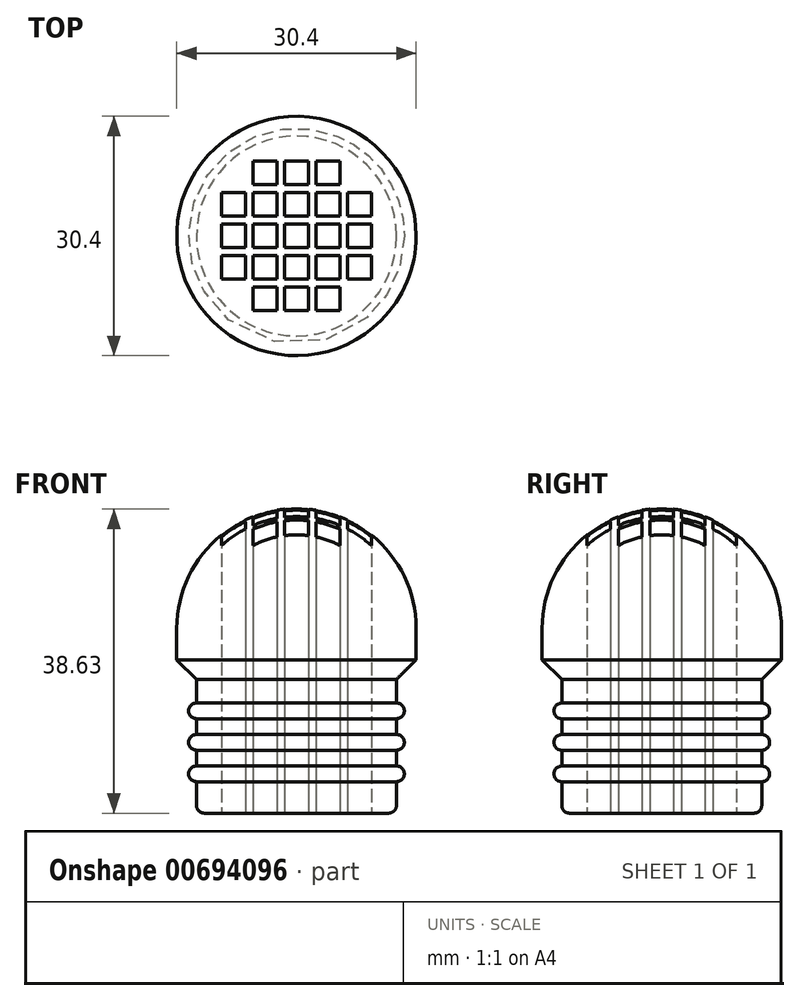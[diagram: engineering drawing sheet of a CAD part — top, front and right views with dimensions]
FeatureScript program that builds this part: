
annotation { "Feature Type Name" : "Feature", "Feature Type Description" : "" }
export const myFeature = defineFeature(function(context is Context, id is Id, definition is map)
    precondition{}
    {
        {
            var Q0;
            Q0=qCreatedBy(makeId("Right.planeOp"),FACE);
            var sketch = newSketch(context, id + "F0", { "sketchPlane" : qUnion([Q0])});
            skLineSegment(sketch, "E0", {"start": v(0, 0) * mm, "end": v(-11.7, 0) * mm});
            skLineSegment(sketch, "E1", {"start": v(-12.7, 1) * mm, "end": v(-12.7, 4) * mm});
            skPoint(sketch, "E2.visualSharp", {"position": v(-12.7, 0) * mm});
            skArc(sketch, "E2.filletArc", {"start": v(-12.7, 1) * mm, "mid": v(-12.4, 0.3) * mm, "end": v(-11.7, 0) * mm});
            skLineSegment(sketch, "E3", {"start": v(-15.2, 23.5) * mm, "end": v(-15.2, 19.5) * mm});
            skLineSegment(sketch, "E4", {"start": v(-15.2, 19.5) * mm, "end": v(-12.7, 17) * mm});
            skArc(sketch, "E5", {"start": v(-15.2, 23.5) * mm, "mid": v(-10.75, 34.25) * mm, "end": v(0, 38.7) * mm});
            skLineSegment(sketch, "E6", {"start": v(0, 38.7) * mm, "end": v(0, 0) * mm});
            skLineSegment(sketch, "E7", {"start": v(-12.7, 14) * mm, "end": v(-12.7, 17) * mm});
            skLineSegment(sketch, "E8", {"start": v(-12.7, 10) * mm, "end": v(-12.7, 12) * mm});
            skLineSegment(sketch, "E9", {"start": v(-12.7, 6) * mm, "end": v(-12.7, 8) * mm});
            skArc(sketch, "E10", {"start": v(-12.7, 14) * mm, "mid": v(-13.7, 13) * mm, "end": v(-12.7, 12) * mm});
            skArc(sketch, "E11", {"start": v(-12.7, 10) * mm, "mid": v(-13.7, 9) * mm, "end": v(-12.7, 8) * mm});
            skArc(sketch, "E12", {"start": v(-12.7, 6) * mm, "mid": v(-13.7, 5) * mm, "end": v(-12.7, 4) * mm});
            skSolve(sketch);
        }
        {
            var Q0;
            Q0 = qSketchRegion(id + "F0", true);
            var Q1;
            Q1 = qConstructionFilter(qBodyType(qCreatedBy(id + "F0" ,EDGE), BodyType.WIRE), ConstructionObject.NO);
            var Q2;
            Q2=sQuery(id+"F0.wireOp",EDGE,"E6");
            revolve(context, id + "F1", {"entities" : qUnion([Q0]), "surfaceEntities" : qUnion([Q1]), "axis" : qUnion([Q2]), "revolveType" : RevolveType.FULL});
        }
        {
            var Q0;
            Q0=makeQuery(id+"F1.opRevolve","SWEPT_FACE",FACE,{"disambiguationData":[OSD([sQuery(id+"F0.wireOp",EDGE,"E0")])]});
            var sketch = newSketch(context, id + "F2", { "sketchPlane" : qUnion([Q0])});
            skLineSegment(sketch, "E13.bottom", {"start": v(-9.5, -6.5) * mm, "end": v(-6.5, -6.5) * mm, "construction": true});
            skLineSegment(sketch, "E13.top", {"start": v(-9.5, -9.5) * mm, "end": v(-6.5, -9.5) * mm, "construction": true});
            skLineSegment(sketch, "E13.left", {"start": v(-9.5, -6.5) * mm, "end": v(-9.5, -9.5) * mm, "construction": true});
            skLineSegment(sketch, "E13.right", {"start": v(-6.5, -6.5) * mm, "end": v(-6.5, -9.5) * mm, "construction": true});
            skPoint(sketch, "E13.middle", {"position": v(-8, -8) * mm});
            skPoint(sketch, "E14.0.1.0", {"position": v(-8, -4) * mm});
            skLineSegment(sketch, "E14.0.1.1", {"start": v(-6.5, -2.5) * mm, "end": v(-6.5, -5.5) * mm});
            skLineSegment(sketch, "E14.0.1.2", {"start": v(-9.5, -5.5) * mm, "end": v(-6.5, -5.5) * mm});
            skLineSegment(sketch, "E14.0.1.3", {"start": v(-9.5, -2.5) * mm, "end": v(-6.5, -2.5) * mm});
            skLineSegment(sketch, "E14.0.1.4", {"start": v(-9.5, -2.5) * mm, "end": v(-9.5, -5.5) * mm});
            skPoint(sketch, "E14.0.2.0", {"position": v(-8, 0) * mm});
            skLineSegment(sketch, "E14.0.2.1", {"start": v(-6.5, 1.5) * mm, "end": v(-6.5, -1.5) * mm});
            skLineSegment(sketch, "E14.0.2.2", {"start": v(-9.5, -1.5) * mm, "end": v(-6.5, -1.5) * mm});
            skLineSegment(sketch, "E14.0.2.3", {"start": v(-9.5, 1.5) * mm, "end": v(-6.5, 1.5) * mm});
            skLineSegment(sketch, "E14.0.2.4", {"start": v(-9.5, 1.5) * mm, "end": v(-9.5, -1.5) * mm});
            skPoint(sketch, "E14.0.3.0", {"position": v(-8, 4) * mm});
            skLineSegment(sketch, "E14.0.3.1", {"start": v(-6.5, 5.5) * mm, "end": v(-6.5, 2.5) * mm});
            skLineSegment(sketch, "E14.0.3.2", {"start": v(-9.5, 2.5) * mm, "end": v(-6.5, 2.5) * mm});
            skLineSegment(sketch, "E14.0.3.3", {"start": v(-9.5, 5.5) * mm, "end": v(-6.5, 5.5) * mm});
            skLineSegment(sketch, "E14.0.3.4", {"start": v(-9.5, 5.5) * mm, "end": v(-9.5, 2.5) * mm});
            skPoint(sketch, "E14.0.4.0", {"position": v(-8, 8) * mm});
            skLineSegment(sketch, "E14.0.4.1", {"start": v(-6.5, 9.5) * mm, "end": v(-6.5, 6.5) * mm, "construction": true});
            skLineSegment(sketch, "E14.0.4.2", {"start": v(-9.5, 6.5) * mm, "end": v(-6.5, 6.5) * mm, "construction": true});
            skLineSegment(sketch, "E14.0.4.3", {"start": v(-9.5, 9.5) * mm, "end": v(-6.5, 9.5) * mm, "construction": true});
            skLineSegment(sketch, "E14.0.4.4", {"start": v(-9.5, 9.5) * mm, "end": v(-9.5, 6.5) * mm, "construction": true});
            skPoint(sketch, "E14.1.0.0", {"position": v(-4, -8) * mm});
            skLineSegment(sketch, "E14.1.0.1", {"start": v(-2.5, -6.5) * mm, "end": v(-2.5, -9.5) * mm});
            skLineSegment(sketch, "E14.1.0.2", {"start": v(-5.5, -9.5) * mm, "end": v(-2.5, -9.5) * mm});
            skLineSegment(sketch, "E14.1.0.3", {"start": v(-5.5, -6.5) * mm, "end": v(-2.5, -6.5) * mm});
            skLineSegment(sketch, "E14.1.0.4", {"start": v(-5.5, -6.5) * mm, "end": v(-5.5, -9.5) * mm});
            skPoint(sketch, "E14.1.1.0", {"position": v(-4, -4) * mm});
            skLineSegment(sketch, "E14.1.1.1", {"start": v(-2.5, -2.5) * mm, "end": v(-2.5, -5.5) * mm});
            skLineSegment(sketch, "E14.1.1.2", {"start": v(-5.5, -5.5) * mm, "end": v(-2.5, -5.5) * mm});
            skLineSegment(sketch, "E14.1.1.3", {"start": v(-5.5, -2.5) * mm, "end": v(-2.5, -2.5) * mm});
            skLineSegment(sketch, "E14.1.1.4", {"start": v(-5.5, -2.5) * mm, "end": v(-5.5, -5.5) * mm});
            skPoint(sketch, "E14.1.2.0", {"position": v(-4, 0) * mm});
            skLineSegment(sketch, "E14.1.2.1", {"start": v(-2.5, 1.5) * mm, "end": v(-2.5, -1.5) * mm});
            skLineSegment(sketch, "E14.1.2.2", {"start": v(-5.5, -1.5) * mm, "end": v(-2.5, -1.5) * mm});
            skLineSegment(sketch, "E14.1.2.3", {"start": v(-5.5, 1.5) * mm, "end": v(-2.5, 1.5) * mm});
            skLineSegment(sketch, "E14.1.2.4", {"start": v(-5.5, 1.5) * mm, "end": v(-5.5, -1.5) * mm});
            skPoint(sketch, "E14.1.3.0", {"position": v(-4, 4) * mm});
            skLineSegment(sketch, "E14.1.3.1", {"start": v(-2.5, 5.5) * mm, "end": v(-2.5, 2.5) * mm});
            skLineSegment(sketch, "E14.1.3.2", {"start": v(-5.5, 2.5) * mm, "end": v(-2.5, 2.5) * mm});
            skLineSegment(sketch, "E14.1.3.3", {"start": v(-5.5, 5.5) * mm, "end": v(-2.5, 5.5) * mm});
            skLineSegment(sketch, "E14.1.3.4", {"start": v(-5.5, 5.5) * mm, "end": v(-5.5, 2.5) * mm});
            skPoint(sketch, "E14.1.4.0", {"position": v(-4, 8) * mm});
            skLineSegment(sketch, "E14.1.4.1", {"start": v(-2.5, 9.5) * mm, "end": v(-2.5, 6.5) * mm});
            skLineSegment(sketch, "E14.1.4.2", {"start": v(-5.5, 6.5) * mm, "end": v(-2.5, 6.5) * mm});
            skLineSegment(sketch, "E14.1.4.3", {"start": v(-5.5, 9.5) * mm, "end": v(-2.5, 9.5) * mm});
            skLineSegment(sketch, "E14.1.4.4", {"start": v(-5.5, 9.5) * mm, "end": v(-5.5, 6.5) * mm});
            skPoint(sketch, "E14.2.0.0", {"position": v(0, -8) * mm});
            skLineSegment(sketch, "E14.2.0.1", {"start": v(1.5, -6.5) * mm, "end": v(1.5, -9.5) * mm});
            skLineSegment(sketch, "E14.2.0.2", {"start": v(-1.5, -9.5) * mm, "end": v(1.5, -9.5) * mm});
            skLineSegment(sketch, "E14.2.0.3", {"start": v(-1.5, -6.5) * mm, "end": v(1.5, -6.5) * mm});
            skLineSegment(sketch, "E14.2.0.4", {"start": v(-1.5, -6.5) * mm, "end": v(-1.5, -9.5) * mm});
            skPoint(sketch, "E14.2.1.0", {"position": v(0, -4) * mm});
            skLineSegment(sketch, "E14.2.1.1", {"start": v(1.5, -2.5) * mm, "end": v(1.5, -5.5) * mm});
            skLineSegment(sketch, "E14.2.1.2", {"start": v(-1.5, -5.5) * mm, "end": v(1.5, -5.5) * mm});
            skLineSegment(sketch, "E14.2.1.3", {"start": v(-1.5, -2.5) * mm, "end": v(1.5, -2.5) * mm});
            skLineSegment(sketch, "E14.2.1.4", {"start": v(-1.5, -2.5) * mm, "end": v(-1.5, -5.5) * mm});
            skPoint(sketch, "E14.2.2.0", {"position": v(0, 0) * mm});
            skLineSegment(sketch, "E14.2.2.1", {"start": v(1.5, 1.5) * mm, "end": v(1.5, -1.5) * mm});
            skLineSegment(sketch, "E14.2.2.2", {"start": v(-1.5, -1.5) * mm, "end": v(1.5, -1.5) * mm});
            skLineSegment(sketch, "E14.2.2.3", {"start": v(-1.5, 1.5) * mm, "end": v(1.5, 1.5) * mm});
            skLineSegment(sketch, "E14.2.2.4", {"start": v(-1.5, 1.5) * mm, "end": v(-1.5, -1.5) * mm});
            skPoint(sketch, "E14.2.3.0", {"position": v(0, 4) * mm});
            skLineSegment(sketch, "E14.2.3.1", {"start": v(1.5, 5.5) * mm, "end": v(1.5, 2.5) * mm});
            skLineSegment(sketch, "E14.2.3.2", {"start": v(-1.5, 2.5) * mm, "end": v(1.5, 2.5) * mm});
            skLineSegment(sketch, "E14.2.3.3", {"start": v(-1.5, 5.5) * mm, "end": v(1.5, 5.5) * mm});
            skLineSegment(sketch, "E14.2.3.4", {"start": v(-1.5, 5.5) * mm, "end": v(-1.5, 2.5) * mm});
            skPoint(sketch, "E14.2.4.0", {"position": v(0, 8) * mm});
            skLineSegment(sketch, "E14.2.4.1", {"start": v(1.5, 9.5) * mm, "end": v(1.5, 6.5) * mm});
            skLineSegment(sketch, "E14.2.4.2", {"start": v(-1.5, 6.5) * mm, "end": v(1.5, 6.5) * mm});
            skLineSegment(sketch, "E14.2.4.3", {"start": v(-1.5, 9.5) * mm, "end": v(1.5, 9.5) * mm});
            skLineSegment(sketch, "E14.2.4.4", {"start": v(-1.5, 9.5) * mm, "end": v(-1.5, 6.5) * mm});
            skPoint(sketch, "E14.3.0.0", {"position": v(4, -8) * mm});
            skLineSegment(sketch, "E14.3.0.1", {"start": v(5.5, -6.5) * mm, "end": v(5.5, -9.5) * mm});
            skLineSegment(sketch, "E14.3.0.2", {"start": v(2.5, -9.5) * mm, "end": v(5.5, -9.5) * mm});
            skLineSegment(sketch, "E14.3.0.3", {"start": v(2.5, -6.5) * mm, "end": v(5.5, -6.5) * mm});
            skLineSegment(sketch, "E14.3.0.4", {"start": v(2.5, -6.5) * mm, "end": v(2.5, -9.5) * mm});
            skPoint(sketch, "E14.3.1.0", {"position": v(4, -4) * mm});
            skLineSegment(sketch, "E14.3.1.1", {"start": v(5.5, -2.5) * mm, "end": v(5.5, -5.5) * mm});
            skLineSegment(sketch, "E14.3.1.2", {"start": v(2.5, -5.5) * mm, "end": v(5.5, -5.5) * mm});
            skLineSegment(sketch, "E14.3.1.3", {"start": v(2.5, -2.5) * mm, "end": v(5.5, -2.5) * mm});
            skLineSegment(sketch, "E14.3.1.4", {"start": v(2.5, -2.5) * mm, "end": v(2.5, -5.5) * mm});
            skPoint(sketch, "E14.3.2.0", {"position": v(4, 0) * mm});
            skLineSegment(sketch, "E14.3.2.1", {"start": v(5.5, 1.5) * mm, "end": v(5.5, -1.5) * mm});
            skLineSegment(sketch, "E14.3.2.2", {"start": v(2.5, -1.5) * mm, "end": v(5.5, -1.5) * mm});
            skLineSegment(sketch, "E14.3.2.3", {"start": v(2.5, 1.5) * mm, "end": v(5.5, 1.5) * mm});
            skLineSegment(sketch, "E14.3.2.4", {"start": v(2.5, 1.5) * mm, "end": v(2.5, -1.5) * mm});
            skPoint(sketch, "E14.3.3.0", {"position": v(4, 4) * mm});
            skLineSegment(sketch, "E14.3.3.1", {"start": v(5.5, 5.5) * mm, "end": v(5.5, 2.5) * mm});
            skLineSegment(sketch, "E14.3.3.2", {"start": v(2.5, 2.5) * mm, "end": v(5.5, 2.5) * mm});
            skLineSegment(sketch, "E14.3.3.3", {"start": v(2.5, 5.5) * mm, "end": v(5.5, 5.5) * mm});
            skLineSegment(sketch, "E14.3.3.4", {"start": v(2.5, 5.5) * mm, "end": v(2.5, 2.5) * mm});
            skPoint(sketch, "E14.3.4.0", {"position": v(4, 8) * mm});
            skLineSegment(sketch, "E14.3.4.1", {"start": v(5.5, 9.5) * mm, "end": v(5.5, 6.5) * mm});
            skLineSegment(sketch, "E14.3.4.2", {"start": v(2.5, 6.5) * mm, "end": v(5.5, 6.5) * mm});
            skLineSegment(sketch, "E14.3.4.3", {"start": v(2.5, 9.5) * mm, "end": v(5.5, 9.5) * mm});
            skLineSegment(sketch, "E14.3.4.4", {"start": v(2.5, 9.5) * mm, "end": v(2.5, 6.5) * mm});
            skPoint(sketch, "E14.4.0.0", {"position": v(8, -8) * mm});
            skLineSegment(sketch, "E14.4.0.1", {"start": v(9.5, -6.5) * mm, "end": v(9.5, -9.5) * mm, "construction": true});
            skLineSegment(sketch, "E14.4.0.2", {"start": v(6.5, -9.5) * mm, "end": v(9.5, -9.5) * mm, "construction": true});
            skLineSegment(sketch, "E14.4.0.3", {"start": v(6.5, -6.5) * mm, "end": v(9.5, -6.5) * mm, "construction": true});
            skLineSegment(sketch, "E14.4.0.4", {"start": v(6.5, -6.5) * mm, "end": v(6.5, -9.5) * mm, "construction": true});
            skPoint(sketch, "E14.4.1.0", {"position": v(8, -4) * mm});
            skLineSegment(sketch, "E14.4.1.1", {"start": v(9.5, -2.5) * mm, "end": v(9.5, -5.5) * mm});
            skLineSegment(sketch, "E14.4.1.2", {"start": v(6.5, -5.5) * mm, "end": v(9.5, -5.5) * mm});
            skLineSegment(sketch, "E14.4.1.3", {"start": v(6.5, -2.5) * mm, "end": v(9.5, -2.5) * mm});
            skLineSegment(sketch, "E14.4.1.4", {"start": v(6.5, -2.5) * mm, "end": v(6.5, -5.5) * mm});
            skPoint(sketch, "E14.4.2.0", {"position": v(8, 0) * mm});
            skLineSegment(sketch, "E14.4.2.1", {"start": v(9.5, 1.5) * mm, "end": v(9.5, -1.5) * mm});
            skLineSegment(sketch, "E14.4.2.2", {"start": v(6.5, -1.5) * mm, "end": v(9.5, -1.5) * mm});
            skLineSegment(sketch, "E14.4.2.3", {"start": v(6.5, 1.5) * mm, "end": v(9.5, 1.5) * mm});
            skLineSegment(sketch, "E14.4.2.4", {"start": v(6.5, 1.5) * mm, "end": v(6.5, -1.5) * mm});
            skPoint(sketch, "E14.4.3.0", {"position": v(8, 4) * mm});
            skLineSegment(sketch, "E14.4.3.1", {"start": v(9.5, 5.5) * mm, "end": v(9.5, 2.5) * mm});
            skLineSegment(sketch, "E14.4.3.2", {"start": v(6.5, 2.5) * mm, "end": v(9.5, 2.5) * mm});
            skLineSegment(sketch, "E14.4.3.3", {"start": v(6.5, 5.5) * mm, "end": v(9.5, 5.5) * mm});
            skLineSegment(sketch, "E14.4.3.4", {"start": v(6.5, 5.5) * mm, "end": v(6.5, 2.5) * mm});
            skPoint(sketch, "E14.4.4.0", {"position": v(8, 8) * mm});
            skLineSegment(sketch, "E14.4.4.1", {"start": v(9.5, 9.5) * mm, "end": v(9.5, 6.5) * mm, "construction": true});
            skLineSegment(sketch, "E14.4.4.2", {"start": v(6.5, 6.5) * mm, "end": v(9.5, 6.5) * mm, "construction": true});
            skLineSegment(sketch, "E14.4.4.3", {"start": v(6.5, 9.5) * mm, "end": v(9.5, 9.5) * mm, "construction": true});
            skLineSegment(sketch, "E14.4.4.4", {"start": v(6.5, 9.5) * mm, "end": v(6.5, 6.5) * mm, "construction": true});
            skLineSegment(sketch, "E14.direction1", {"start": v(-9.5, -9.5) * mm, "end": v(-5.5, -9.5) * mm, "construction": true});
            skLineSegment(sketch, "E14.direction2", {"start": v(-9.5, -9.5) * mm, "end": v(-9.5, -5.5) * mm, "construction": true});
            skSolve(sketch);
        }
        {
            var Q0;
            Q0 = qSketchRegion(id + "F2", true);
            extrude(context, id + "F3", {"entities" : qUnion([Q0]), "operationType" : NewBodyOperationType.REMOVE, "oppositeDirection" : true, "depth" : 50 * mm, "offsetDistance" : 25 * mm});
        }
    });
